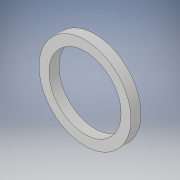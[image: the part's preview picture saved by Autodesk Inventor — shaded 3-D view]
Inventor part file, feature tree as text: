
AUTODESK INVENTOR PART (.ipt)
format: ipt  version: 2019 (Build 230136000, 136)  size: 103,936 bytes
history: native  units: mm
features: extrude x2, sketch x2
ambient origin geometry x8: Origin, YZ Plane, XZ Plane, XY Plane, X Axis, Y Axis, Z Axis, Center Point
bodies: Solid1 (feature_tree)
feature tree (4):
  extrude  "Extrusion1"  Depth=40.0mm TaperAngle=0.0deg
  extrude  "Extrusion2"  Depth=4.0mm TaperAngle=0.0deg
  sketch  "Sketch1"  dims[d0=370.0mm d1=40.0mm d2=0.0mm]
  sketch  "Sketch3"  dims[d3=290.0mm d4=4.0mm d5=0.0mm]
